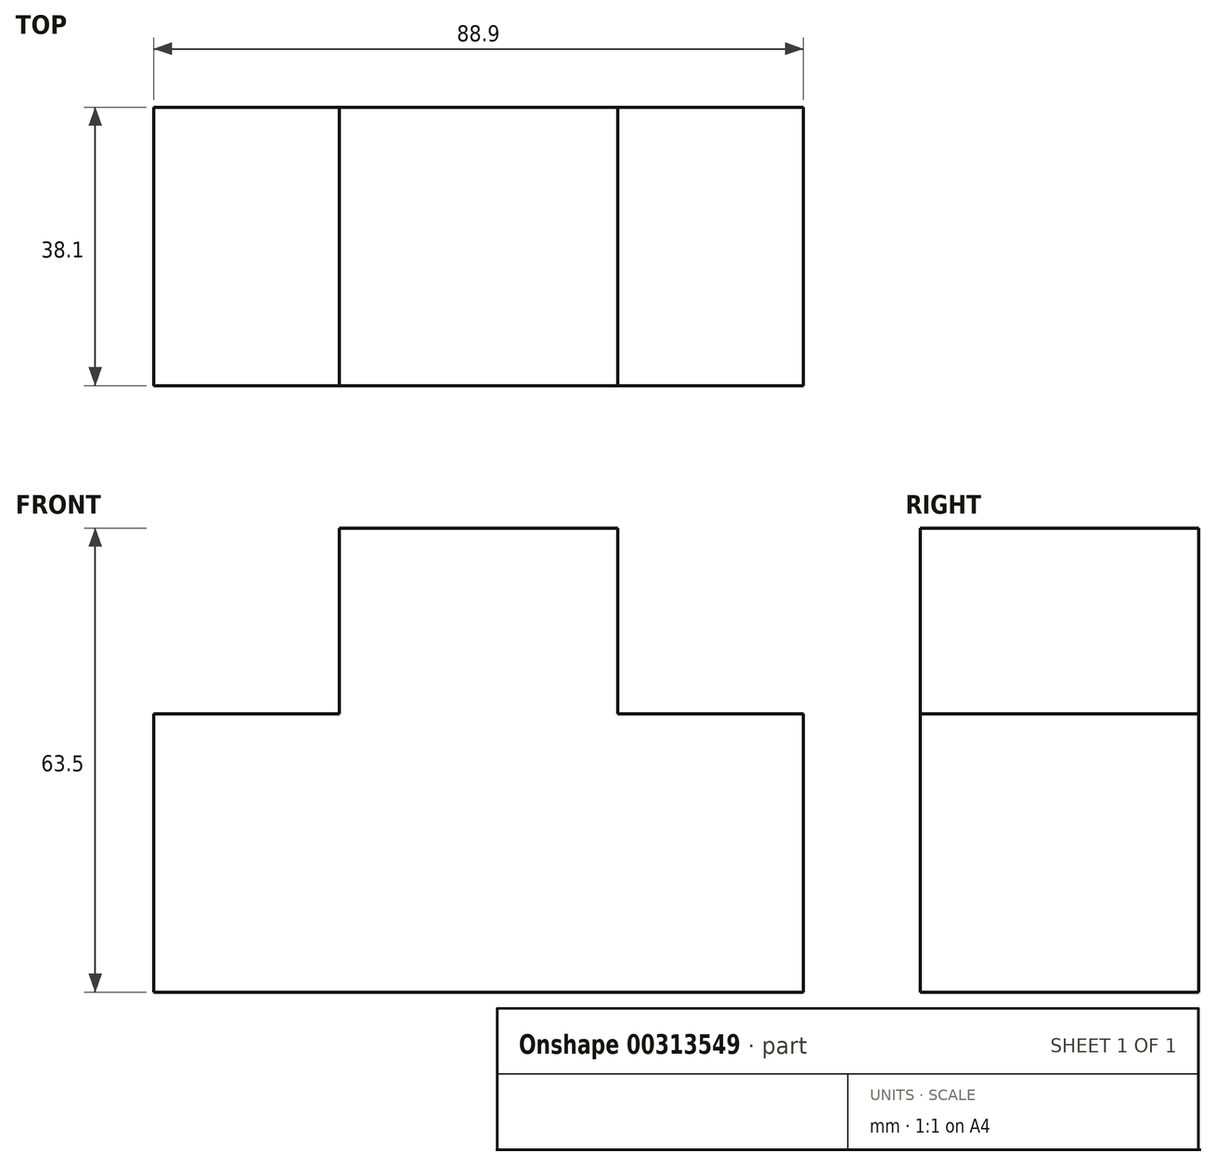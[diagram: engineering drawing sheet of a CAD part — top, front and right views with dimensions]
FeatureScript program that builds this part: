
annotation { "Feature Type Name" : "Feature", "Feature Type Description" : "" }
export const myFeature = defineFeature(function(context is Context, id is Id, definition is map)
    precondition{}
    {
        {
            var Q0;
            Q0=qCreatedBy(makeId("Front.planeOp"),FACE);
            var sketch = newSketch(context, id + "F0", { "sketchPlane" : qUnion([Q0])});
            skLineSegment(sketch, "E0", {"start": v(-38.18, -34.98) * mm, "end": v(50.72, -34.98) * mm});
            skLineSegment(sketch, "E1", {"start": v(50.72, -34.98) * mm, "end": v(50.72, 3.12) * mm});
            skLineSegment(sketch, "E2", {"start": v(50.72, 3.12) * mm, "end": v(25.32, 3.12) * mm});
            skLineSegment(sketch, "E3", {"start": v(25.32, 3.12) * mm, "end": v(25.32, 28.52) * mm});
            skLineSegment(sketch, "E4", {"start": v(25.32, 28.52) * mm, "end": v(-12.78, 28.52) * mm});
            skLineSegment(sketch, "E5", {"start": v(-12.78, 28.52) * mm, "end": v(-12.78, 3.12) * mm});
            skLineSegment(sketch, "E6", {"start": v(-12.78, 3.12) * mm, "end": v(-38.18, 3.12) * mm});
            skLineSegment(sketch, "E7", {"start": v(-38.18, 3.12) * mm, "end": v(-38.18, -34.98) * mm});
            skSolve(sketch);
        }
        {
            var Q0;
            Q0=makeQuery(id+"F0.imprint","IMPRINT",FACE,{"disambiguationData":[TD([[makeQuery(id+"F0.imprint","IMPRINT",EDGE,{"derivedFrom":sQuery(id+"F0.wireOp",EDGE,"E0")}),1.0]])]});
            extrude(context, id + "F1", {"entities" : qUnion([Q0]), "depth" : 38.1 * mm});
        }
    });
